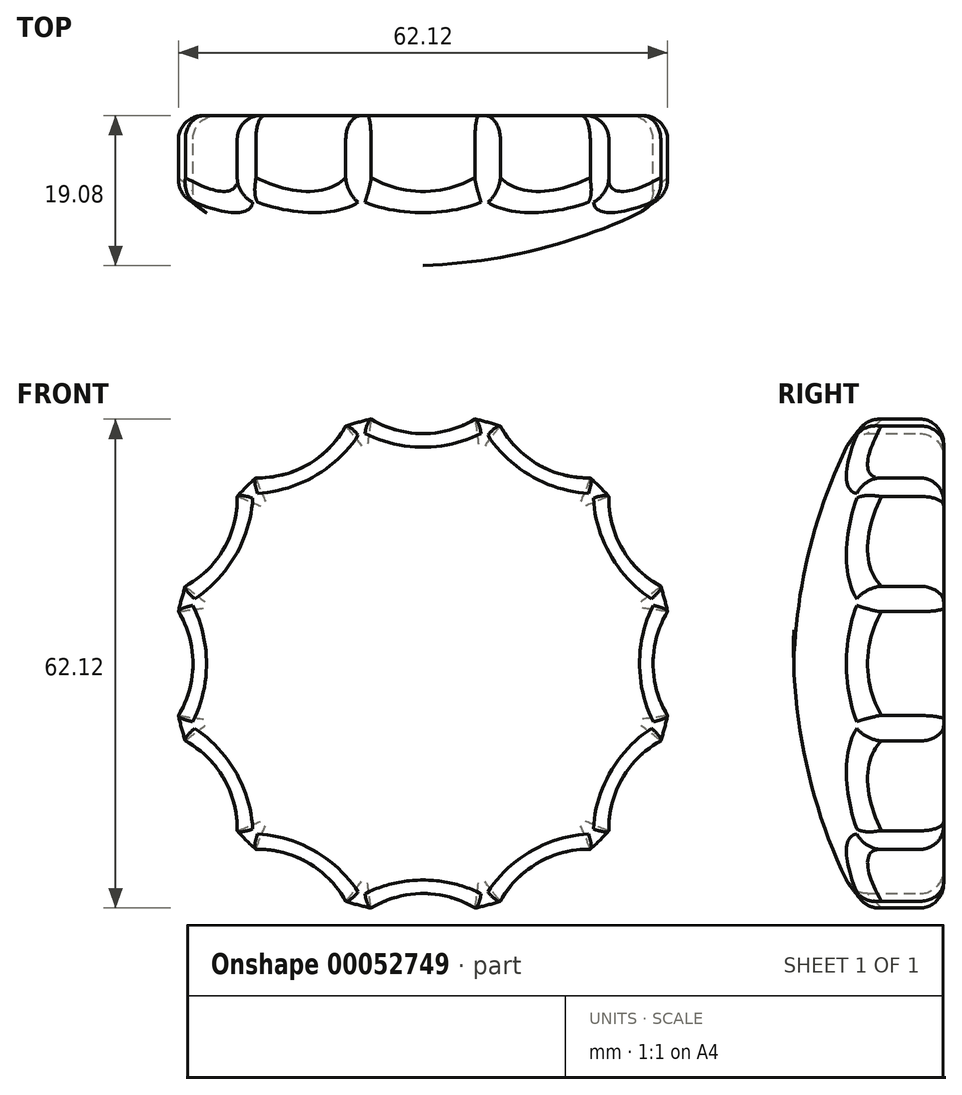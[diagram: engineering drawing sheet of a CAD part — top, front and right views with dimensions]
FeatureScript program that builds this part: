
annotation { "Feature Type Name" : "Feature", "Feature Type Description" : "" }
export const myFeature = defineFeature(function(context is Context, id is Id, definition is map)
    precondition{}
    {
        {
            var Q0;
            Q0=qCreatedBy(makeId("Right.planeOp"),FACE);
            var sketch = newSketch(context, id + "F0", { "sketchPlane" : qUnion([Q0])});
            skLineSegment(sketch, "E0.bottom", {"start": v(0, 0) * mm, "end": v(-19.05, 0) * mm});
            skLineSegment(sketch, "E0.top", {"start": v(0, 31.75) * mm, "end": v(-10.16, 31.75) * mm});
            skLineSegment(sketch, "E0.left", {"start": v(0, 0) * mm, "end": v(0, 31.75) * mm});
            skPoint(sketch, "E1.orphan", {"position": v(-5.53, 0) * mm});
            skArc(sketch, "E2", {"start": v(-10.16, 31.75) * mm, "mid": v(-16.53, 16.42) * mm, "end": v(-19.05, 0) * mm});
            skSolve(sketch);
        }
        {
            var Q0;
            Q0=makeQuery(id+"F0.imprint","IMPRINT",FACE,{"disambiguationData":[TD([[makeQuery(id+"F0.imprint","IMPRINT",EDGE,{"derivedFrom":sQuery(id+"F0.wireOp",EDGE,"E0.bottom")}),-1.0]])]});
            var Q1;
            Q1=sQuery(id+"F0.wireOp",EDGE,"E0.bottom");
            revolve(context, id + "F1", {"entities" : qUnion([Q0]), "axis" : qUnion([Q1]), "revolveType" : RevolveType.FULL});
        }
        {
            var Q0;
            Q0=qCreatedBy(makeId("Front.planeOp"),FACE);
            var sketch = newSketch(context, id + "F2", { "sketchPlane" : qUnion([Q0])});
            skCircle(sketch, "E3", {"center": v(-41.91, 0) * mm, "radius": 12.7 * mm});
            skCircle(sketch, "E4", {"center": v(0, 0) * mm, "radius": 41.91 * mm, "construction": true});
            skCircle(sketch, "E5", {"center": v(0, 0) * mm, "radius": 54.61 * mm, "construction": true});
            skCircle(sketch, "E6", {"center": v(0, 41.91) * mm, "radius": 12.7 * mm});
            skCircle(sketch, "E7", {"center": v(41.91, 0) * mm, "radius": 12.7 * mm});
            skCircle(sketch, "E8", {"center": v(0, -41.91) * mm, "radius": 12.7 * mm});
            skLineSegment(sketch, "E9", {"start": v(67.3, -38.86) * mm, "end": v(0, 0) * mm, "construction": true});
            skLineSegment(sketch, "E10", {"start": v(33.25, -57.58) * mm, "end": v(0, 0) * mm, "construction": true});
            skLineSegment(sketch, "E11", {"start": v(0, 0) * mm, "end": v(-107.5, 0) * mm});
            skCircle(sketch, "E12", {"center": v(-36.3, 20.95) * mm, "radius": 12.7 * mm});
            skCircle(sketch, "E13", {"center": v(-20.96, 36.3) * mm, "radius": 12.7 * mm});
            skCircle(sketch, "E14", {"center": v(20.96, -36.3) * mm, "radius": 12.7 * mm});
            skCircle(sketch, "E15", {"center": v(36.3, -20.95) * mm, "radius": 12.7 * mm});
            skLineSegment(sketch, "E16", {"start": v(39.45, 68.32) * mm, "end": v(0, 0) * mm, "construction": true});
            skLineSegment(sketch, "E17", {"start": v(71.1, 41.05) * mm, "end": v(0, 0) * mm, "construction": true});
            skCircle(sketch, "E18", {"center": v(-36.3, -20.96) * mm, "radius": 12.7 * mm});
            skCircle(sketch, "E19", {"center": v(-20.95, -36.3) * mm, "radius": 12.7 * mm});
            skCircle(sketch, "E20", {"center": v(20.95, 36.3) * mm, "radius": 12.7 * mm});
            skCircle(sketch, "E21", {"center": v(36.3, 20.96) * mm, "radius": 12.7 * mm});
            skSolve(sketch);
        }
        {
            var Q0;
            Q0=qSketchRegion(id+"F2",true);
            extrude(context, id + "F3", {"entities" : qUnion([Q0]), "operationType" : NewBodyOperationType.REMOVE, "depth" : 38.1 * mm});
        }
        {
            var Q0;
            Q0=makeQuery(id+"F1.opRevolve","SWEPT_FACE",FACE,{"disambiguationData":[OSD([sQuery(id+"F0.wireOp",EDGE,"E2")])]});
            fillet(context, id + "F4", {"entities" : qUnion([Q0]), "radius" : 3 * mm, "tangentPropagation" : true, "allowEdgeOverflow" : false});
        }
        {
            var Q0;
            Q0=makeQuery(id+"F1.opRevolve","SWEPT_FACE",FACE,{"disambiguationData":[OSD([sQuery(id+"F0.wireOp",EDGE,"E0.left")])]});
            fillet(context, id + "F5", {"entities" : qUnion([Q0]), "radius" : 3 * mm, "tangentPropagation" : true, "allowEdgeOverflow" : false});
        }
    });
